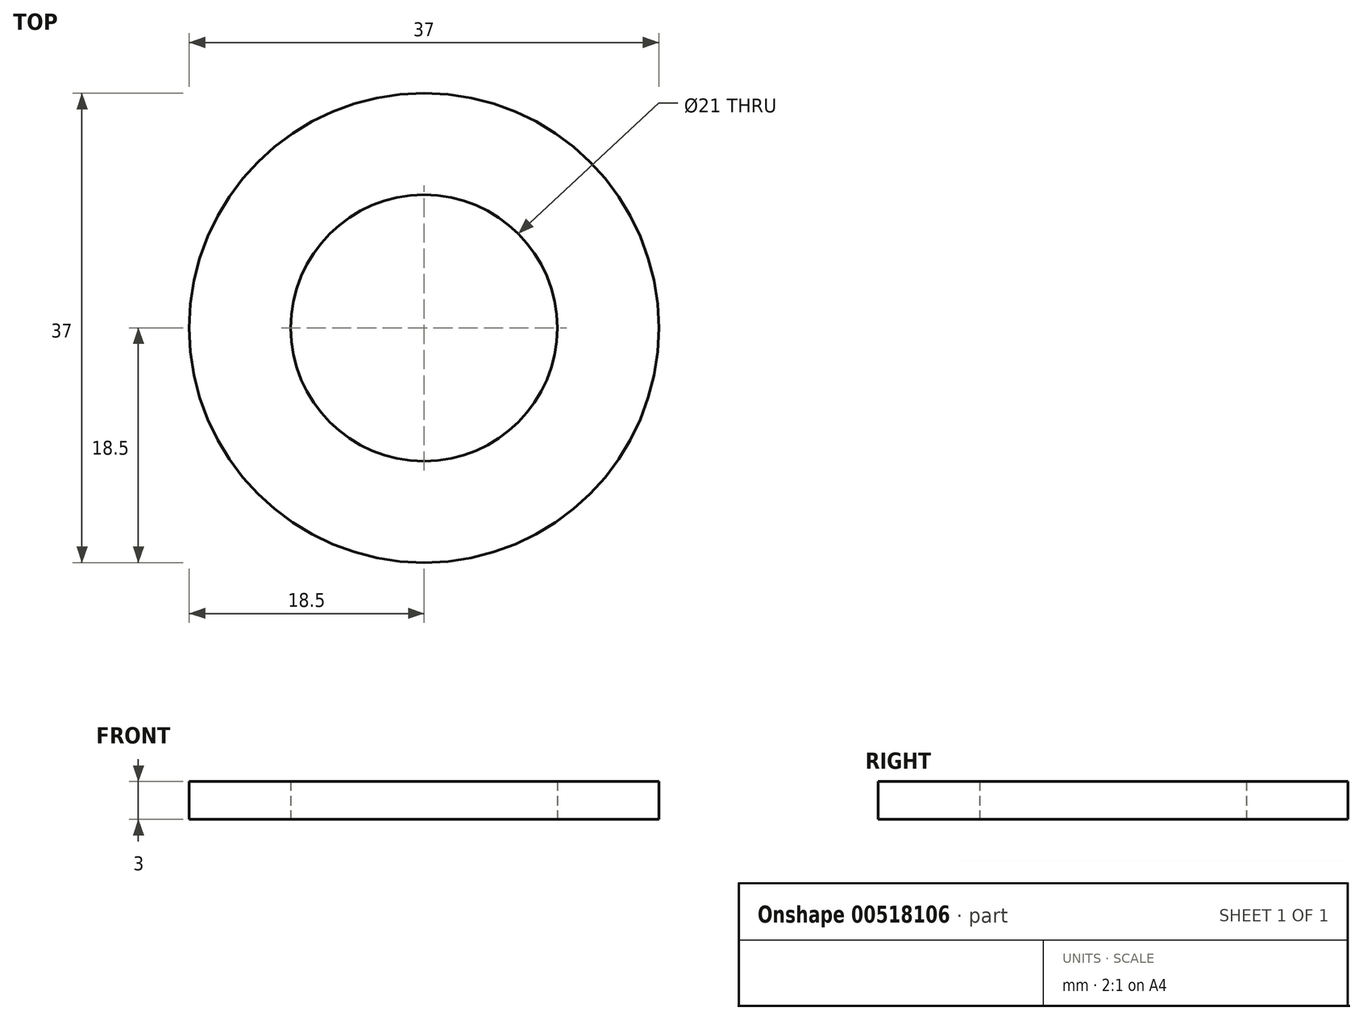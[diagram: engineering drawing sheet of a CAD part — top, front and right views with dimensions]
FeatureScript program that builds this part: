
annotation { "Feature Type Name" : "Feature", "Feature Type Description" : "" }
export const myFeature = defineFeature(function(context is Context, id is Id, definition is map)
    precondition{}
    {
        {
            assignVariable(context, id + "F0", {"name" : "s", "anyValue" : 3});
        }
        {
            var Q0;
            Q0=qCreatedBy(makeId("Top.planeOp"),FACE);
            var sketch = newSketch(context, id + "F1", { "sketchPlane" : qUnion([Q0])});
            skCircle(sketch, "E0", {"center": v(0, 0) * mm, "radius": 10.5 * mm});
            skCircle(sketch, "E1", {"center": v(0, 0) * mm, "radius": 18.5 * mm});
            skSolve(sketch);
        }
        {
            var Q0;
            Q0=makeQuery(id+"F1.imprint","IMPRINT",FACE,{"disambiguationData":[TD([[makeQuery(id+"F1.imprint","IMPRINT",EDGE,{"derivedFrom":sQuery(id+"F1.wireOp",EDGE,"E0")}),-1.0]])]});
            extrude(context, id + "F2", {"entities" : qUnion([Q0]), "depth" : (getVariable(context, 's')) * mm, "offsetDistance" : 25 * mm});
        }
    });
